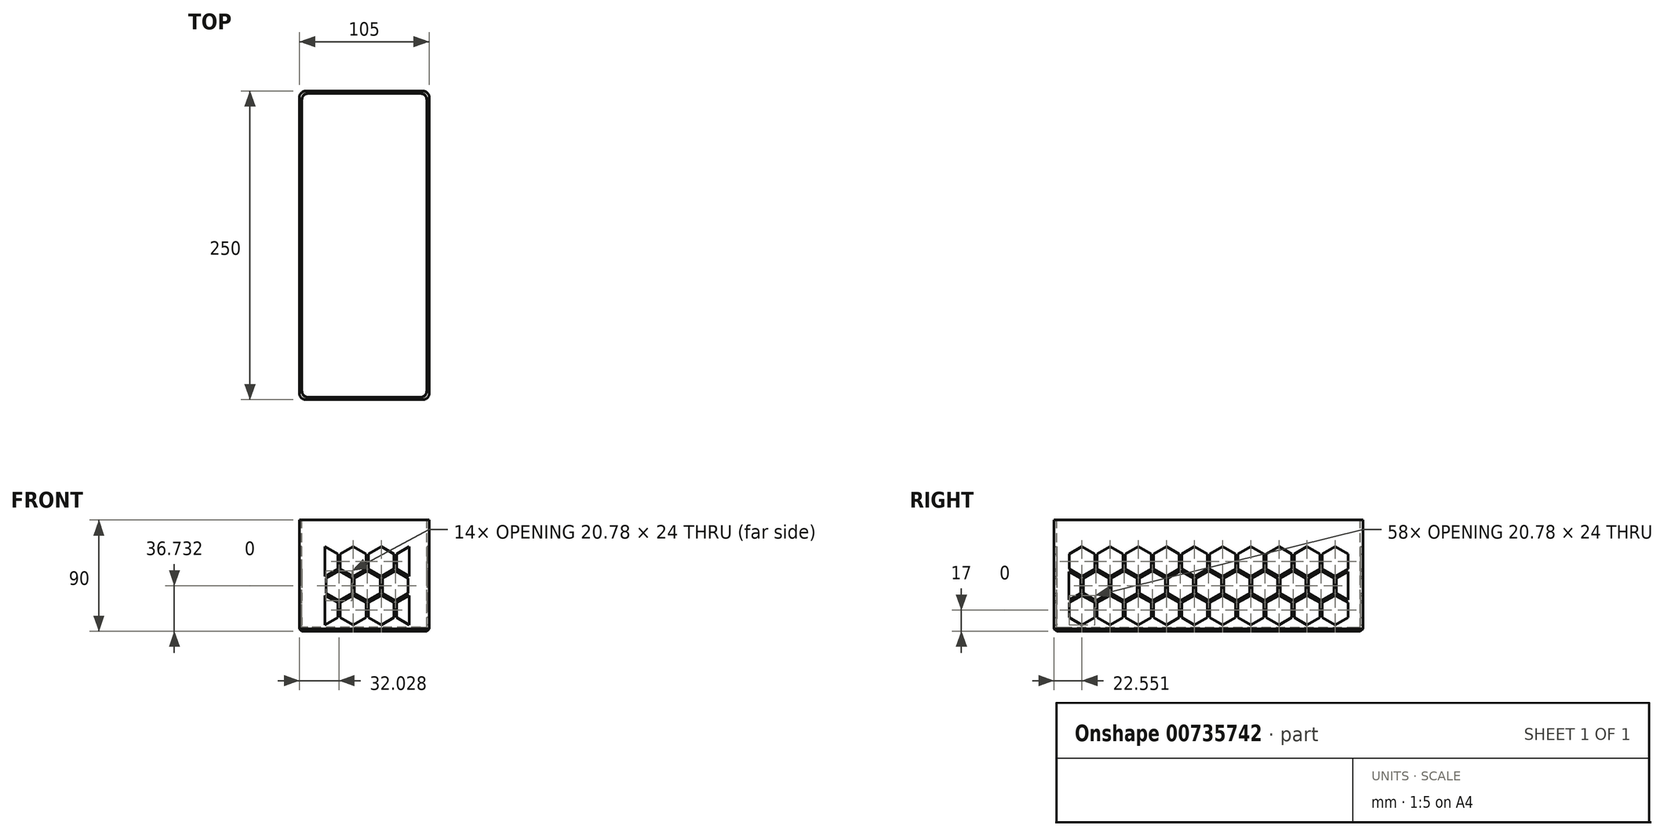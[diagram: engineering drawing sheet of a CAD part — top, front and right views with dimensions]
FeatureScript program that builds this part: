
annotation { "Feature Type Name" : "Feature", "Feature Type Description" : "" }
export const myFeature = defineFeature(function(context is Context, id is Id, definition is map)
    precondition{}
    {
        {
            var Q0;
            Q0=qCreatedBy(makeId("Top.planeOp"),FACE);
            var sketch = newSketch(context, id + "F0", { "sketchPlane" : qUnion([Q0])});
            skLineSegment(sketch, "E0.bottom", {"start": v(-56.87, 197.97) * mm, "end": v(48.13, 197.97) * mm});
            skLineSegment(sketch, "E0.top", {"start": v(-56.87, -52.03) * mm, "end": v(48.13, -52.03) * mm});
            skLineSegment(sketch, "E0.left", {"start": v(-56.87, 197.97) * mm, "end": v(-56.87, -52.03) * mm});
            skLineSegment(sketch, "E0.right", {"start": v(48.13, 197.97) * mm, "end": v(48.13, -52.03) * mm});
            skSolve(sketch);
        }
        {
            var Q0;
            Q0 = qSketchRegion(id + "F0", true);
            extrude(context, id + "F1", {"entities" : qUnion([Q0]), "depth" : 90 * mm, "offsetDistance" : 25 * mm});
        }
        {
            var Q0;
            Q0=makeQuery(id+"F1.opExtrude","CAP_FACE",FACE,{"disambiguationData":[OSD([sQuery(id+"F0.wireOp",EDGE,"E0.bottom"),sQuery(id+"F0.wireOp",EDGE,"E0.top"),sQuery(id+"F0.wireOp",EDGE,"E0.left"),sQuery(id+"F0.wireOp",EDGE,"E0.right")])],"isStart":false});
            var sketch = newSketch(context, id + "F2", { "sketchPlane" : qUnion([Q0])});
            skLineSegment(sketch, "E1.bottom", {"start": v(46.13, -50.03) * mm, "end": v(-54.87, -50.03) * mm});
            skLineSegment(sketch, "E1.top", {"start": v(46.13, 195.97) * mm, "end": v(-54.87, 195.97) * mm});
            skLineSegment(sketch, "E1.left", {"start": v(46.13, -50.03) * mm, "end": v(46.13, 195.97) * mm});
            skLineSegment(sketch, "E1.right", {"start": v(-54.87, -50.03) * mm, "end": v(-54.87, 195.97) * mm});
            skSolve(sketch);
        }
        {
            var Q0;
            Q0 = qSketchRegion(id + "F2", true);
            extrude(context, id + "F3", {"entities" : qUnion([Q0]), "operationType" : NewBodyOperationType.REMOVE, "oppositeDirection" : true, "depth" : 87 * mm, "offsetDistance" : 25 * mm});
        }
        {
            var Q0;
            Q0=makeQuery(id+"F1.opExtrude","SWEPT_EDGE",EDGE,{"disambiguationData":[OSD([sQuery(id+"F0.wireOp",EDGE,"E0.top"),sQuery(id+"F0.wireOp",EDGE,"E0.right")])]});
            var Q1;
            Q1=makeQuery(id+"F1.opExtrude","SWEPT_EDGE",EDGE,{"disambiguationData":[OSD([sQuery(id+"F0.wireOp",EDGE,"E0.top"),sQuery(id+"F0.wireOp",EDGE,"E0.left")])]});
            var Q2;
            Q2=makeQuery(id+"F1.opExtrude","SWEPT_EDGE",EDGE,{"disambiguationData":[OSD([sQuery(id+"F0.wireOp",EDGE,"E0.bottom"),sQuery(id+"F0.wireOp",EDGE,"E0.right")])]});
            var Q3;
            Q3=makeQuery(id+"F1.opExtrude","SWEPT_EDGE",EDGE,{"disambiguationData":[OSD([sQuery(id+"F0.wireOp",EDGE,"E0.bottom"),sQuery(id+"F0.wireOp",EDGE,"E0.left")])]});
            fillet(context, id + "F4", {"entities" : qUnion([Q0, Q1, Q2, Q3]), "radius" : 5 * mm, "tangentPropagation" : true, "allowEdgeOverflow" : false});
        }
        {
            var Q0;
            Q0=makeQuery(id+"F3.boolean.opBoolean","COPY",EDGE,{"derivedFrom":makeQuery(id+"F3.opExtrude","SWEPT_EDGE",EDGE,{"disambiguationData":[OSD([sQuery(id+"F2.wireOp",EDGE,"E1.top"),sQuery(id+"F2.wireOp",EDGE,"E1.right")])]})});
            var Q1;
            Q1=makeQuery(id+"F3.boolean.opBoolean","COPY",EDGE,{"derivedFrom":makeQuery(id+"F3.opExtrude","SWEPT_EDGE",EDGE,{"disambiguationData":[OSD([sQuery(id+"F2.wireOp",EDGE,"E1.top"),sQuery(id+"F2.wireOp",EDGE,"E1.left")])]})});
            var Q2;
            Q2=makeQuery(id+"F3.boolean.opBoolean","COPY",EDGE,{"derivedFrom":makeQuery(id+"F3.opExtrude","SWEPT_EDGE",EDGE,{"disambiguationData":[OSD([sQuery(id+"F2.wireOp",EDGE,"E1.bottom"),sQuery(id+"F2.wireOp",EDGE,"E1.right")])]})});
            var Q3;
            Q3=makeQuery(id+"F3.boolean.opBoolean","COPY",EDGE,{"derivedFrom":makeQuery(id+"F3.opExtrude","SWEPT_EDGE",EDGE,{"disambiguationData":[OSD([sQuery(id+"F2.wireOp",EDGE,"E1.bottom"),sQuery(id+"F2.wireOp",EDGE,"E1.left")])]})});
            fillet(context, id + "F5", {"entities" : qUnion([Q0, Q1, Q2, Q3]), "radius" : 5 * mm, "tangentPropagation" : true, "allowEdgeOverflow" : false});
        }
        {
            var Q0;
            Q0=makeQuery(id+"F1.opExtrude","CAP_FACE",FACE,{"disambiguationData":[OSD([sQuery(id+"F0.wireOp",EDGE,"E0.bottom"),sQuery(id+"F0.wireOp",EDGE,"E0.top"),sQuery(id+"F0.wireOp",EDGE,"E0.left"),sQuery(id+"F0.wireOp",EDGE,"E0.right")])],"isStart":true});
            chamfer(context, id + "F6", {"entities" : qUnion([Q0]), "width" : 2 * mm, "tangentPropagation" : true});
        }
        {
            var Q0;
            Q0=makeQuery(id+"F1.opExtrude","SWEPT_FACE",FACE,{"disambiguationData":[OSD([sQuery(id+"F0.wireOp",EDGE,"E0.left")])]});
            var sketch = newSketch(context, id + "F7", { "sketchPlane" : qUnion([Q0])});
            skLineSegment(sketch, "E2", {"start": v(-185.97, 68.46) * mm, "end": v(-185.97, -21.54) * mm, "construction": true});
            skLineSegment(sketch, "E3", {"start": v(-185.97, 68.46) * mm, "end": v(74.03, 68.46) * mm, "construction": true});
            skLineSegment(sketch, "E4", {"start": v(40.03, 68.46) * mm, "end": v(40.03, -21.54) * mm});
            skCircle(sketch, "E5.cCircle", {"center": v(-175.58, 56.46) * mm, "radius": 10.4 * mm, "construction": true});
            skLineSegment(sketch, "E5.0", {"start": v(-165.2, 50.46) * mm, "end": v(-175.58, 44.46) * mm});
            skLineSegment(sketch, "E5.1", {"start": v(-175.58, 44.46) * mm, "end": v(-185.97, 50.46) * mm});
            skLineSegment(sketch, "E5.2", {"start": v(-185.97, 50.46) * mm, "end": v(-185.97, 62.46) * mm});
            skLineSegment(sketch, "E5.3", {"start": v(-185.97, 62.46) * mm, "end": v(-175.58, 68.46) * mm});
            skLineSegment(sketch, "E5.4", {"start": v(-175.58, 68.46) * mm, "end": v(-165.2, 62.46) * mm});
            skLineSegment(sketch, "E5.5", {"start": v(-165.2, 62.46) * mm, "end": v(-165.2, 50.46) * mm});
            skPoint(sketch, "E5.0.midPoint", {"position": v(-170.39, 47.46) * mm});
            skCircle(sketch, "E6.cCircle", {"center": v(-152.8, 56.46) * mm, "radius": 10.4 * mm, "construction": true});
            skLineSegment(sketch, "E6.0", {"start": v(-142.4, 50.46) * mm, "end": v(-152.8, 44.46) * mm});
            skLineSegment(sketch, "E6.1", {"start": v(-152.8, 44.46) * mm, "end": v(-163.2, 50.46) * mm});
            skLineSegment(sketch, "E6.2", {"start": v(-163.2, 50.46) * mm, "end": v(-163.2, 62.46) * mm});
            skLineSegment(sketch, "E6.3", {"start": v(-163.2, 62.46) * mm, "end": v(-152.8, 68.46) * mm});
            skLineSegment(sketch, "E6.4", {"start": v(-152.8, 68.46) * mm, "end": v(-142.4, 62.46) * mm});
            skLineSegment(sketch, "E6.5", {"start": v(-142.4, 62.46) * mm, "end": v(-142.4, 50.46) * mm});
            skPoint(sketch, "E6.0.midPoint", {"position": v(-147.6, 47.46) * mm});
            skLineSegment(sketch, "E7", {"start": v(68.97, 44.46) * mm, "end": v(-241.4, 44.46) * mm, "construction": true});
            skCircle(sketch, "E8.cCircle", {"center": v(-130.01, 56.46) * mm, "radius": 10.4 * mm, "construction": true});
            skLineSegment(sketch, "E8.0", {"start": v(-119.62, 50.46) * mm, "end": v(-130.01, 44.46) * mm});
            skLineSegment(sketch, "E8.1", {"start": v(-130.01, 44.46) * mm, "end": v(-140.4, 50.46) * mm});
            skLineSegment(sketch, "E8.2", {"start": v(-140.4, 50.46) * mm, "end": v(-140.4, 62.46) * mm});
            skLineSegment(sketch, "E8.3", {"start": v(-140.4, 62.46) * mm, "end": v(-130.01, 68.46) * mm});
            skLineSegment(sketch, "E8.4", {"start": v(-130.01, 68.46) * mm, "end": v(-119.62, 62.46) * mm});
            skLineSegment(sketch, "E8.5", {"start": v(-119.62, 62.46) * mm, "end": v(-119.62, 50.46) * mm});
            skPoint(sketch, "E8.0.midPoint", {"position": v(-124.82, 47.46) * mm});
            skCircle(sketch, "E9.cCircle", {"center": v(-107.23, 56.46) * mm, "radius": 10.4 * mm, "construction": true});
            skLineSegment(sketch, "E9.0", {"start": v(-96.84, 50.46) * mm, "end": v(-107.23, 44.46) * mm});
            skLineSegment(sketch, "E9.1", {"start": v(-107.23, 44.46) * mm, "end": v(-117.62, 50.46) * mm});
            skLineSegment(sketch, "E9.2", {"start": v(-117.62, 50.46) * mm, "end": v(-117.62, 62.46) * mm});
            skLineSegment(sketch, "E9.3", {"start": v(-117.62, 62.46) * mm, "end": v(-107.23, 68.46) * mm});
            skLineSegment(sketch, "E9.4", {"start": v(-107.23, 68.46) * mm, "end": v(-96.84, 62.46) * mm});
            skLineSegment(sketch, "E9.5", {"start": v(-96.84, 62.46) * mm, "end": v(-96.84, 50.46) * mm});
            skPoint(sketch, "E9.0.midPoint", {"position": v(-102.03, 47.46) * mm});
            skCircle(sketch, "E10.cCircle", {"center": v(-84.44, 56.46) * mm, "radius": 10.4 * mm, "construction": true});
            skLineSegment(sketch, "E10.0", {"start": v(-74.05, 50.46) * mm, "end": v(-84.44, 44.46) * mm});
            skLineSegment(sketch, "E10.1", {"start": v(-84.44, 44.46) * mm, "end": v(-94.84, 50.46) * mm});
            skLineSegment(sketch, "E10.2", {"start": v(-94.84, 50.46) * mm, "end": v(-94.84, 62.46) * mm});
            skLineSegment(sketch, "E10.3", {"start": v(-94.84, 62.46) * mm, "end": v(-84.44, 68.46) * mm});
            skLineSegment(sketch, "E10.4", {"start": v(-84.44, 68.46) * mm, "end": v(-74.05, 62.46) * mm});
            skLineSegment(sketch, "E10.5", {"start": v(-74.05, 62.46) * mm, "end": v(-74.05, 50.46) * mm});
            skPoint(sketch, "E10.0.midPoint", {"position": v(-79.25, 47.46) * mm});
            skCircle(sketch, "E11.cCircle", {"center": v(-61.66, 56.46) * mm, "radius": 10.4 * mm, "construction": true});
            skLineSegment(sketch, "E11.0", {"start": v(-51.27, 50.46) * mm, "end": v(-61.66, 44.46) * mm});
            skLineSegment(sketch, "E11.1", {"start": v(-61.66, 44.46) * mm, "end": v(-72.05, 50.46) * mm});
            skLineSegment(sketch, "E11.2", {"start": v(-72.05, 50.46) * mm, "end": v(-72.05, 62.46) * mm});
            skLineSegment(sketch, "E11.3", {"start": v(-72.05, 62.46) * mm, "end": v(-61.66, 68.46) * mm});
            skLineSegment(sketch, "E11.4", {"start": v(-61.66, 68.46) * mm, "end": v(-51.27, 62.46) * mm});
            skLineSegment(sketch, "E11.5", {"start": v(-51.27, 62.46) * mm, "end": v(-51.27, 50.46) * mm});
            skPoint(sketch, "E11.0.midPoint", {"position": v(-56.46, 47.46) * mm});
            skCircle(sketch, "E12.cCircle", {"center": v(-38.87, 56.46) * mm, "radius": 10.4 * mm, "construction": true});
            skLineSegment(sketch, "E12.0", {"start": v(-28.48, 50.46) * mm, "end": v(-38.87, 44.46) * mm});
            skLineSegment(sketch, "E12.1", {"start": v(-38.87, 44.46) * mm, "end": v(-49.27, 50.46) * mm});
            skLineSegment(sketch, "E12.2", {"start": v(-49.27, 50.46) * mm, "end": v(-49.27, 62.46) * mm});
            skLineSegment(sketch, "E12.3", {"start": v(-49.27, 62.46) * mm, "end": v(-38.87, 68.46) * mm});
            skLineSegment(sketch, "E12.4", {"start": v(-38.87, 68.46) * mm, "end": v(-28.48, 62.46) * mm});
            skLineSegment(sketch, "E12.5", {"start": v(-28.48, 62.46) * mm, "end": v(-28.48, 50.46) * mm});
            skPoint(sketch, "E12.0.midPoint", {"position": v(-33.68, 47.46) * mm});
            skCircle(sketch, "E13.cCircle", {"center": v(-16.1, 56.46) * mm, "radius": 10.4 * mm, "construction": true});
            skLineSegment(sketch, "E13.0", {"start": v(-5.7, 50.46) * mm, "end": v(-16.1, 44.46) * mm});
            skLineSegment(sketch, "E13.1", {"start": v(-16.1, 44.46) * mm, "end": v(-26.48, 50.46) * mm});
            skLineSegment(sketch, "E13.2", {"start": v(-26.48, 50.46) * mm, "end": v(-26.48, 62.46) * mm});
            skLineSegment(sketch, "E13.3", {"start": v(-26.48, 62.46) * mm, "end": v(-16.1, 68.46) * mm});
            skLineSegment(sketch, "E13.4", {"start": v(-16.1, 68.46) * mm, "end": v(-5.7, 62.46) * mm});
            skLineSegment(sketch, "E13.5", {"start": v(-5.7, 62.46) * mm, "end": v(-5.7, 50.46) * mm});
            skPoint(sketch, "E13.0.midPoint", {"position": v(-10.9, 47.46) * mm});
            skCircle(sketch, "E14.cCircle", {"center": v(6.7, 56.46) * mm, "radius": 10.4 * mm, "construction": true});
            skLineSegment(sketch, "E14.0", {"start": v(17.09, 50.46) * mm, "end": v(6.7, 44.46) * mm});
            skLineSegment(sketch, "E14.1", {"start": v(6.7, 44.46) * mm, "end": v(-3.7, 50.46) * mm});
            skLineSegment(sketch, "E14.2", {"start": v(-3.7, 50.46) * mm, "end": v(-3.7, 62.46) * mm});
            skLineSegment(sketch, "E14.3", {"start": v(-3.7, 62.46) * mm, "end": v(6.7, 68.46) * mm});
            skLineSegment(sketch, "E14.4", {"start": v(6.7, 68.46) * mm, "end": v(17.09, 62.46) * mm});
            skLineSegment(sketch, "E14.5", {"start": v(17.09, 62.46) * mm, "end": v(17.09, 50.46) * mm});
            skPoint(sketch, "E14.0.midPoint", {"position": v(11.9, 47.46) * mm});
            skCircle(sketch, "E15.cCircle", {"center": v(29.48, 56.46) * mm, "radius": 10.4 * mm, "construction": true});
            skLineSegment(sketch, "E15.0", {"start": v(39.87, 50.46) * mm, "end": v(29.48, 44.46) * mm});
            skLineSegment(sketch, "E15.1", {"start": v(29.48, 44.46) * mm, "end": v(19.09, 50.46) * mm});
            skLineSegment(sketch, "E15.2", {"start": v(19.09, 50.46) * mm, "end": v(19.09, 62.46) * mm});
            skLineSegment(sketch, "E15.3", {"start": v(19.09, 62.46) * mm, "end": v(29.48, 68.46) * mm});
            skLineSegment(sketch, "E15.4", {"start": v(29.48, 68.46) * mm, "end": v(39.87, 62.46) * mm});
            skLineSegment(sketch, "E15.5", {"start": v(39.87, 62.46) * mm, "end": v(39.87, 50.46) * mm});
            skPoint(sketch, "E15.0.midPoint", {"position": v(34.68, 47.46) * mm});
            skArc(sketch, "E16.cCircle", {"start": v(-185.97, 26.39) * mm, "mid": v(-176.58, 36.73) * mm, "end": v(-185.97, 47.08) * mm, "construction": true});
            skLineSegment(sketch, "E16.0", {"start": v(-176.58, 30.73) * mm, "end": v(-185.97, 25.3) * mm});
            skLineSegment(sketch, "E16.4", {"start": v(-185.97, 48.15) * mm, "end": v(-176.58, 42.73) * mm});
            skLineSegment(sketch, "E16.5", {"start": v(-176.58, 42.73) * mm, "end": v(-176.58, 30.73) * mm});
            skPoint(sketch, "E16.0.midPoint", {"position": v(-181.78, 27.73) * mm});
            skCircle(sketch, "E17.cCircle", {"center": v(-141.4, 36.73) * mm, "radius": 10.4 * mm, "construction": true});
            skLineSegment(sketch, "E17.0", {"start": v(-131.01, 30.73) * mm, "end": v(-141.4, 24.73) * mm});
            skLineSegment(sketch, "E17.1", {"start": v(-141.4, 24.73) * mm, "end": v(-151.8, 30.73) * mm});
            skLineSegment(sketch, "E17.2", {"start": v(-151.8, 30.73) * mm, "end": v(-151.8, 42.73) * mm});
            skLineSegment(sketch, "E17.3", {"start": v(-151.8, 42.73) * mm, "end": v(-141.4, 48.73) * mm});
            skLineSegment(sketch, "E17.4", {"start": v(-141.4, 48.73) * mm, "end": v(-131.01, 42.73) * mm});
            skLineSegment(sketch, "E17.5", {"start": v(-131.01, 42.73) * mm, "end": v(-131.01, 30.73) * mm});
            skPoint(sketch, "E17.0.midPoint", {"position": v(-136.2, 27.73) * mm});
            skCircle(sketch, "E18.cCircle", {"center": v(-118.62, 36.73) * mm, "radius": 10.4 * mm, "construction": true});
            skLineSegment(sketch, "E18.0", {"start": v(-108.23, 30.73) * mm, "end": v(-118.62, 24.73) * mm});
            skLineSegment(sketch, "E18.1", {"start": v(-118.62, 24.73) * mm, "end": v(-129.01, 30.73) * mm});
            skLineSegment(sketch, "E18.2", {"start": v(-129.01, 30.73) * mm, "end": v(-129.01, 42.73) * mm});
            skLineSegment(sketch, "E18.3", {"start": v(-129.01, 42.73) * mm, "end": v(-118.62, 48.73) * mm});
            skLineSegment(sketch, "E18.4", {"start": v(-118.62, 48.73) * mm, "end": v(-108.23, 42.73) * mm});
            skLineSegment(sketch, "E18.5", {"start": v(-108.23, 42.73) * mm, "end": v(-108.23, 30.73) * mm});
            skPoint(sketch, "E18.0.midPoint", {"position": v(-113.42, 27.73) * mm});
            skCircle(sketch, "E19.cCircle", {"center": v(-95.84, 36.73) * mm, "radius": 10.4 * mm, "construction": true});
            skLineSegment(sketch, "E19.0", {"start": v(-85.44, 30.73) * mm, "end": v(-95.84, 24.73) * mm});
            skLineSegment(sketch, "E19.1", {"start": v(-95.84, 24.73) * mm, "end": v(-106.23, 30.73) * mm});
            skLineSegment(sketch, "E19.2", {"start": v(-106.23, 30.73) * mm, "end": v(-106.23, 42.73) * mm});
            skLineSegment(sketch, "E19.3", {"start": v(-106.23, 42.73) * mm, "end": v(-95.84, 48.73) * mm});
            skLineSegment(sketch, "E19.4", {"start": v(-95.84, 48.73) * mm, "end": v(-85.44, 42.73) * mm});
            skLineSegment(sketch, "E19.5", {"start": v(-85.44, 42.73) * mm, "end": v(-85.44, 30.73) * mm});
            skPoint(sketch, "E19.0.midPoint", {"position": v(-90.64, 27.73) * mm});
            skCircle(sketch, "E20.cCircle", {"center": v(-73.05, 36.73) * mm, "radius": 10.4 * mm, "construction": true});
            skLineSegment(sketch, "E20.0", {"start": v(-62.66, 30.73) * mm, "end": v(-73.05, 24.73) * mm});
            skLineSegment(sketch, "E20.1", {"start": v(-73.05, 24.73) * mm, "end": v(-83.44, 30.73) * mm});
            skLineSegment(sketch, "E20.2", {"start": v(-83.44, 30.73) * mm, "end": v(-83.44, 42.73) * mm});
            skLineSegment(sketch, "E20.3", {"start": v(-83.44, 42.73) * mm, "end": v(-73.05, 48.73) * mm});
            skLineSegment(sketch, "E20.4", {"start": v(-73.05, 48.73) * mm, "end": v(-62.66, 42.73) * mm});
            skLineSegment(sketch, "E20.5", {"start": v(-62.66, 42.73) * mm, "end": v(-62.66, 30.73) * mm});
            skPoint(sketch, "E20.0.midPoint", {"position": v(-67.86, 27.73) * mm});
            skCircle(sketch, "E21.cCircle", {"center": v(-50.27, 36.73) * mm, "radius": 10.4 * mm, "construction": true});
            skLineSegment(sketch, "E21.0", {"start": v(-39.87, 30.73) * mm, "end": v(-50.27, 24.73) * mm});
            skLineSegment(sketch, "E21.1", {"start": v(-50.27, 24.73) * mm, "end": v(-60.66, 30.73) * mm});
            skLineSegment(sketch, "E21.2", {"start": v(-60.66, 30.73) * mm, "end": v(-60.66, 42.73) * mm});
            skLineSegment(sketch, "E21.3", {"start": v(-60.66, 42.73) * mm, "end": v(-50.27, 48.73) * mm});
            skLineSegment(sketch, "E21.4", {"start": v(-50.27, 48.73) * mm, "end": v(-39.87, 42.73) * mm});
            skLineSegment(sketch, "E21.5", {"start": v(-39.87, 42.73) * mm, "end": v(-39.87, 30.73) * mm});
            skPoint(sketch, "E21.0.midPoint", {"position": v(-45.07, 27.73) * mm});
            skCircle(sketch, "E22.cCircle", {"center": v(-27.48, 36.73) * mm, "radius": 10.4 * mm, "construction": true});
            skLineSegment(sketch, "E22.0", {"start": v(-17.1, 30.73) * mm, "end": v(-27.48, 24.73) * mm});
            skLineSegment(sketch, "E22.1", {"start": v(-27.48, 24.73) * mm, "end": v(-37.87, 30.73) * mm});
            skLineSegment(sketch, "E22.2", {"start": v(-37.87, 30.73) * mm, "end": v(-37.87, 42.73) * mm});
            skLineSegment(sketch, "E22.3", {"start": v(-37.87, 42.73) * mm, "end": v(-27.48, 48.73) * mm});
            skLineSegment(sketch, "E22.4", {"start": v(-27.48, 48.73) * mm, "end": v(-17.1, 42.73) * mm});
            skLineSegment(sketch, "E22.5", {"start": v(-17.1, 42.73) * mm, "end": v(-17.1, 30.73) * mm});
            skPoint(sketch, "E22.0.midPoint", {"position": v(-22.29, 27.73) * mm});
            skCircle(sketch, "E23.cCircle", {"center": v(-4.7, 36.73) * mm, "radius": 10.4 * mm, "construction": true});
            skLineSegment(sketch, "E23.0", {"start": v(5.7, 30.73) * mm, "end": v(-4.7, 24.73) * mm});
            skLineSegment(sketch, "E23.1", {"start": v(-4.7, 24.73) * mm, "end": v(-15.1, 30.73) * mm});
            skLineSegment(sketch, "E23.2", {"start": v(-15.1, 30.73) * mm, "end": v(-15.1, 42.73) * mm});
            skLineSegment(sketch, "E23.3", {"start": v(-15.1, 42.73) * mm, "end": v(-4.7, 48.73) * mm});
            skLineSegment(sketch, "E23.4", {"start": v(-4.7, 48.73) * mm, "end": v(5.7, 42.73) * mm});
            skLineSegment(sketch, "E23.5", {"start": v(5.7, 42.73) * mm, "end": v(5.7, 30.73) * mm});
            skPoint(sketch, "E23.0.midPoint", {"position": v(0.5, 27.73) * mm});
            skCircle(sketch, "E24.cCircle", {"center": v(18.09, 36.73) * mm, "radius": 10.4 * mm, "construction": true});
            skLineSegment(sketch, "E24.0", {"start": v(28.48, 30.73) * mm, "end": v(18.09, 24.73) * mm});
            skLineSegment(sketch, "E24.1", {"start": v(18.09, 24.73) * mm, "end": v(7.7, 30.73) * mm});
            skLineSegment(sketch, "E24.2", {"start": v(7.7, 30.73) * mm, "end": v(7.7, 42.73) * mm});
            skLineSegment(sketch, "E24.3", {"start": v(7.7, 42.73) * mm, "end": v(18.09, 48.73) * mm});
            skLineSegment(sketch, "E24.4", {"start": v(18.09, 48.73) * mm, "end": v(28.48, 42.73) * mm});
            skLineSegment(sketch, "E24.5", {"start": v(28.48, 42.73) * mm, "end": v(28.48, 30.73) * mm});
            skPoint(sketch, "E24.0.midPoint", {"position": v(23.28, 27.73) * mm});
            skLineSegment(sketch, "E25", {"start": v(74.03, 48.73) * mm, "end": v(-185.97, 48.73) * mm, "construction": true});
            skCircle(sketch, "E26.cCircle", {"center": v(-164.2, 36.73) * mm, "radius": 10.4 * mm, "construction": true});
            skLineSegment(sketch, "E26.0", {"start": v(-153.8, 30.73) * mm, "end": v(-164.2, 24.73) * mm});
            skLineSegment(sketch, "E26.1", {"start": v(-164.2, 24.73) * mm, "end": v(-174.58, 30.73) * mm});
            skLineSegment(sketch, "E26.2", {"start": v(-174.58, 30.73) * mm, "end": v(-174.58, 42.73) * mm});
            skLineSegment(sketch, "E26.3", {"start": v(-174.58, 42.73) * mm, "end": v(-164.2, 48.73) * mm});
            skLineSegment(sketch, "E26.4", {"start": v(-164.2, 48.73) * mm, "end": v(-153.8, 42.73) * mm});
            skLineSegment(sketch, "E26.5", {"start": v(-153.8, 42.73) * mm, "end": v(-153.8, 30.73) * mm});
            skPoint(sketch, "E26.0.midPoint", {"position": v(-159, 27.73) * mm});
            skLineSegment(sketch, "E27", {"start": v(-189.97, 24.73) * mm, "end": v(75.25, 24.73) * mm, "construction": true});
            skArc(sketch, "E28.cCircle", {"start": v(40.03, 47.09) * mm, "mid": v(30.48, 36.73) * mm, "end": v(40.03, 26.37) * mm, "construction": true});
            skLineSegment(sketch, "E28.1", {"start": v(40.87, 24.73) * mm, "end": v(30.48, 30.73) * mm});
            skLineSegment(sketch, "E28.2", {"start": v(30.48, 30.73) * mm, "end": v(30.48, 42.73) * mm});
            skLineSegment(sketch, "E28.3", {"start": v(30.48, 42.73) * mm, "end": v(40.03, 48.24) * mm});
            skPoint(sketch, "E28.0.midPoint", {"position": v(46.07, 27.73) * mm});
            skCircle(sketch, "E29.cCircle", {"center": v(-175.58, 17) * mm, "radius": 10.4 * mm, "construction": true});
            skLineSegment(sketch, "E29.0", {"start": v(-165.2, 11) * mm, "end": v(-175.58, 5) * mm});
            skLineSegment(sketch, "E29.1", {"start": v(-175.58, 5) * mm, "end": v(-185.97, 11) * mm});
            skLineSegment(sketch, "E29.2", {"start": v(-185.97, 11) * mm, "end": v(-185.97, 23) * mm});
            skLineSegment(sketch, "E29.3", {"start": v(-185.97, 23) * mm, "end": v(-175.58, 29) * mm});
            skLineSegment(sketch, "E29.4", {"start": v(-175.58, 29) * mm, "end": v(-165.2, 23) * mm});
            skLineSegment(sketch, "E29.5", {"start": v(-165.2, 23) * mm, "end": v(-165.2, 11) * mm});
            skPoint(sketch, "E29.0.midPoint", {"position": v(-170.39, 8) * mm});
            skLineSegment(sketch, "E30", {"start": v(-185.97, 29) * mm, "end": v(74.03, 29) * mm, "construction": true});
            skLineSegment(sketch, "E31", {"start": v(-185.97, 5) * mm, "end": v(74.03, 5) * mm, "construction": true});
            skCircle(sketch, "E32.cCircle", {"center": v(-152.8, 17) * mm, "radius": 10.4 * mm, "construction": true});
            skLineSegment(sketch, "E32.0", {"start": v(-142.4, 11) * mm, "end": v(-152.8, 5) * mm});
            skLineSegment(sketch, "E32.1", {"start": v(-152.8, 5) * mm, "end": v(-163.2, 11) * mm});
            skLineSegment(sketch, "E32.2", {"start": v(-163.2, 11) * mm, "end": v(-163.2, 23) * mm});
            skLineSegment(sketch, "E32.3", {"start": v(-163.2, 23) * mm, "end": v(-152.8, 29) * mm});
            skLineSegment(sketch, "E32.4", {"start": v(-152.8, 29) * mm, "end": v(-142.4, 23) * mm});
            skLineSegment(sketch, "E32.5", {"start": v(-142.4, 23) * mm, "end": v(-142.4, 11) * mm});
            skPoint(sketch, "E32.0.midPoint", {"position": v(-147.6, 8) * mm});
            skCircle(sketch, "E33.cCircle", {"center": v(-130.01, 17) * mm, "radius": 10.4 * mm, "construction": true});
            skLineSegment(sketch, "E33.0", {"start": v(-119.62, 11) * mm, "end": v(-130.01, 5) * mm});
            skLineSegment(sketch, "E33.1", {"start": v(-130.01, 5) * mm, "end": v(-140.4, 11) * mm});
            skLineSegment(sketch, "E33.2", {"start": v(-140.4, 11) * mm, "end": v(-140.4, 23) * mm});
            skLineSegment(sketch, "E33.3", {"start": v(-140.4, 23) * mm, "end": v(-130.01, 29) * mm});
            skLineSegment(sketch, "E33.4", {"start": v(-130.01, 29) * mm, "end": v(-119.62, 23) * mm});
            skLineSegment(sketch, "E33.5", {"start": v(-119.62, 23) * mm, "end": v(-119.62, 11) * mm});
            skPoint(sketch, "E33.0.midPoint", {"position": v(-124.82, 8) * mm});
            skCircle(sketch, "E34.cCircle", {"center": v(-107.23, 17) * mm, "radius": 10.4 * mm, "construction": true});
            skLineSegment(sketch, "E34.0", {"start": v(-96.84, 11) * mm, "end": v(-107.23, 5) * mm});
            skLineSegment(sketch, "E34.1", {"start": v(-107.23, 5) * mm, "end": v(-117.62, 11) * mm});
            skLineSegment(sketch, "E34.2", {"start": v(-117.62, 11) * mm, "end": v(-117.62, 23) * mm});
            skLineSegment(sketch, "E34.3", {"start": v(-117.62, 23) * mm, "end": v(-107.23, 29) * mm});
            skLineSegment(sketch, "E34.4", {"start": v(-107.23, 29) * mm, "end": v(-96.84, 23) * mm});
            skLineSegment(sketch, "E34.5", {"start": v(-96.84, 23) * mm, "end": v(-96.84, 11) * mm});
            skPoint(sketch, "E34.0.midPoint", {"position": v(-102.03, 8) * mm});
            skCircle(sketch, "E35.cCircle", {"center": v(-84.44, 17) * mm, "radius": 10.4 * mm, "construction": true});
            skLineSegment(sketch, "E35.0", {"start": v(-74.05, 11) * mm, "end": v(-84.44, 5) * mm});
            skLineSegment(sketch, "E35.1", {"start": v(-84.44, 5) * mm, "end": v(-94.84, 11) * mm});
            skLineSegment(sketch, "E35.2", {"start": v(-94.84, 11) * mm, "end": v(-94.84, 23) * mm});
            skLineSegment(sketch, "E35.3", {"start": v(-94.84, 23) * mm, "end": v(-84.44, 29) * mm});
            skLineSegment(sketch, "E35.4", {"start": v(-84.44, 29) * mm, "end": v(-74.05, 23) * mm});
            skLineSegment(sketch, "E35.5", {"start": v(-74.05, 23) * mm, "end": v(-74.05, 11) * mm});
            skPoint(sketch, "E35.0.midPoint", {"position": v(-79.25, 8) * mm});
            skCircle(sketch, "E36.cCircle", {"center": v(-61.66, 17) * mm, "radius": 10.4 * mm, "construction": true});
            skLineSegment(sketch, "E36.0", {"start": v(-51.27, 11) * mm, "end": v(-61.66, 5) * mm});
            skLineSegment(sketch, "E36.1", {"start": v(-61.66, 5) * mm, "end": v(-72.05, 11) * mm});
            skLineSegment(sketch, "E36.2", {"start": v(-72.05, 11) * mm, "end": v(-72.05, 23) * mm});
            skLineSegment(sketch, "E36.3", {"start": v(-72.05, 23) * mm, "end": v(-61.66, 29) * mm});
            skLineSegment(sketch, "E36.4", {"start": v(-61.66, 29) * mm, "end": v(-51.27, 23) * mm});
            skLineSegment(sketch, "E36.5", {"start": v(-51.27, 23) * mm, "end": v(-51.27, 11) * mm});
            skPoint(sketch, "E36.0.midPoint", {"position": v(-56.46, 8) * mm});
            skCircle(sketch, "E37.cCircle", {"center": v(-38.87, 17) * mm, "radius": 10.4 * mm, "construction": true});
            skLineSegment(sketch, "E37.0", {"start": v(-28.48, 11) * mm, "end": v(-38.87, 5) * mm});
            skLineSegment(sketch, "E37.1", {"start": v(-38.87, 5) * mm, "end": v(-49.27, 11) * mm});
            skLineSegment(sketch, "E37.2", {"start": v(-49.27, 11) * mm, "end": v(-49.27, 23) * mm});
            skLineSegment(sketch, "E37.3", {"start": v(-49.27, 23) * mm, "end": v(-38.87, 29) * mm});
            skLineSegment(sketch, "E37.4", {"start": v(-38.87, 29) * mm, "end": v(-28.48, 23) * mm});
            skLineSegment(sketch, "E37.5", {"start": v(-28.48, 23) * mm, "end": v(-28.48, 11) * mm});
            skPoint(sketch, "E37.0.midPoint", {"position": v(-33.68, 8) * mm});
            skCircle(sketch, "E38.cCircle", {"center": v(-16.1, 17) * mm, "radius": 10.4 * mm, "construction": true});
            skLineSegment(sketch, "E38.0", {"start": v(-5.7, 11) * mm, "end": v(-16.1, 5) * mm});
            skLineSegment(sketch, "E38.1", {"start": v(-16.1, 5) * mm, "end": v(-26.48, 11) * mm});
            skLineSegment(sketch, "E38.2", {"start": v(-26.48, 11) * mm, "end": v(-26.48, 23) * mm});
            skLineSegment(sketch, "E38.3", {"start": v(-26.48, 23) * mm, "end": v(-16.1, 29) * mm});
            skLineSegment(sketch, "E38.4", {"start": v(-16.1, 29) * mm, "end": v(-5.7, 23) * mm});
            skLineSegment(sketch, "E38.5", {"start": v(-5.7, 23) * mm, "end": v(-5.7, 11) * mm});
            skPoint(sketch, "E38.0.midPoint", {"position": v(-10.9, 8) * mm});
            skCircle(sketch, "E39.cCircle", {"center": v(6.7, 17) * mm, "radius": 10.4 * mm, "construction": true});
            skLineSegment(sketch, "E39.0", {"start": v(17.09, 11) * mm, "end": v(6.7, 5) * mm});
            skLineSegment(sketch, "E39.1", {"start": v(6.7, 5) * mm, "end": v(-3.7, 11) * mm});
            skLineSegment(sketch, "E39.2", {"start": v(-3.7, 11) * mm, "end": v(-3.7, 23) * mm});
            skLineSegment(sketch, "E39.3", {"start": v(-3.7, 23) * mm, "end": v(6.7, 29) * mm});
            skLineSegment(sketch, "E39.4", {"start": v(6.7, 29) * mm, "end": v(17.09, 23) * mm});
            skLineSegment(sketch, "E39.5", {"start": v(17.09, 23) * mm, "end": v(17.09, 11) * mm});
            skPoint(sketch, "E39.0.midPoint", {"position": v(11.9, 8) * mm});
            skCircle(sketch, "E40.cCircle", {"center": v(29.48, 17) * mm, "radius": 10.4 * mm, "construction": true});
            skLineSegment(sketch, "E40.0", {"start": v(39.87, 11) * mm, "end": v(29.48, 5) * mm});
            skLineSegment(sketch, "E40.1", {"start": v(29.48, 5) * mm, "end": v(19.09, 11) * mm});
            skLineSegment(sketch, "E40.2", {"start": v(19.09, 11) * mm, "end": v(19.09, 23) * mm});
            skLineSegment(sketch, "E40.3", {"start": v(19.09, 23) * mm, "end": v(29.48, 29) * mm});
            skLineSegment(sketch, "E40.4", {"start": v(29.48, 29) * mm, "end": v(39.87, 23) * mm});
            skLineSegment(sketch, "E40.5", {"start": v(39.87, 23) * mm, "end": v(39.87, 11) * mm});
            skPoint(sketch, "E40.0.midPoint", {"position": v(34.68, 8) * mm});
            skPoint(sketch, "E41.orphan", {"position": v(-197.37, 30.73) * mm});
            skPoint(sketch, "E42.orphan", {"position": v(-186.97, 24.73) * mm});
            skPoint(sketch, "E43.orphan", {"position": v(51.26, 42.73) * mm});
            skPoint(sketch, "E28.0.start.orphan", {"position": v(51.26, 30.73) * mm});
            skPoint(sketch, "E44.orphan", {"position": v(40.87, 48.73) * mm});
            skPoint(sketch, "E45.orphan", {"position": v(-186.97, 48.73) * mm});
            skLineSegment(sketch, "E46", {"start": v(-185.97, 48.15) * mm, "end": v(-185.97, 25.3) * mm});
            skSolve(sketch);
        }
        {
            var Q0;
            Q0 = qSketchRegion(id + "F7", true);
            extrude(context, id + "F8", {"entities" : qUnion([Q0]), "operationType" : NewBodyOperationType.REMOVE, "oppositeDirection" : true, "depth" : 120 * mm, "offsetDistance" : 25 * mm});
        }
        {
            var Q0;
            Q0=makeQuery(id+"F1.opExtrude","SWEPT_FACE",FACE,{"disambiguationData":[OSD([sQuery(id+"F0.wireOp",EDGE,"E0.bottom")])]});
            var sketch = newSketch(context, id + "F9", { "sketchPlane" : qUnion([Q0])});
            skLineSegment(sketch, "E47", {"start": v(-133.65, 68.46) * mm, "end": v(-133.65, -21.54) * mm, "construction": true});
            skLineSegment(sketch, "E48", {"start": v(-133.65, 68.46) * mm, "end": v(126.35, 68.46) * mm, "construction": true});
            skLineSegment(sketch, "E49", {"start": v(92.35, 68.46) * mm, "end": v(92.35, -21.54) * mm});
            skLineSegment(sketch, "E50.0", {"start": v(-21.73, 50.46) * mm, "end": v(-32.12, 44.46) * mm});
            skLineSegment(sketch, "E50.4", {"start": v(-32.12, 68.46) * mm, "end": v(-21.73, 62.46) * mm});
            skLineSegment(sketch, "E50.5", {"start": v(-21.73, 62.46) * mm, "end": v(-21.73, 50.46) * mm});
            skCircle(sketch, "E51.cCircle", {"center": v(-9.33, 56.46) * mm, "radius": 10.4 * mm, "construction": true});
            skLineSegment(sketch, "E51.0", {"start": v(1.06, 50.46) * mm, "end": v(-9.33, 44.46) * mm});
            skLineSegment(sketch, "E51.1", {"start": v(-9.33, 44.46) * mm, "end": v(-19.73, 50.46) * mm});
            skLineSegment(sketch, "E51.2", {"start": v(-19.73, 50.46) * mm, "end": v(-19.73, 62.46) * mm});
            skLineSegment(sketch, "E51.3", {"start": v(-19.73, 62.46) * mm, "end": v(-9.33, 68.46) * mm});
            skLineSegment(sketch, "E51.4", {"start": v(-9.33, 68.46) * mm, "end": v(1.06, 62.46) * mm});
            skLineSegment(sketch, "E51.5", {"start": v(1.06, 62.46) * mm, "end": v(1.06, 50.46) * mm});
            skPoint(sketch, "E51.0.midPoint", {"position": v(-4.14, 47.46) * mm});
            skCircle(sketch, "E52.cCircle", {"center": v(13.45, 56.46) * mm, "radius": 10.4 * mm, "construction": true});
            skLineSegment(sketch, "E52.0", {"start": v(23.84, 50.46) * mm, "end": v(13.45, 44.46) * mm});
            skLineSegment(sketch, "E52.1", {"start": v(13.45, 44.46) * mm, "end": v(3.06, 50.46) * mm});
            skLineSegment(sketch, "E52.2", {"start": v(3.06, 50.46) * mm, "end": v(3.06, 62.46) * mm});
            skLineSegment(sketch, "E52.3", {"start": v(3.06, 62.46) * mm, "end": v(13.45, 68.46) * mm});
            skLineSegment(sketch, "E52.4", {"start": v(13.45, 68.46) * mm, "end": v(23.84, 62.46) * mm});
            skLineSegment(sketch, "E52.5", {"start": v(23.84, 62.46) * mm, "end": v(23.84, 50.46) * mm});
            skPoint(sketch, "E52.0.midPoint", {"position": v(18.65, 47.46) * mm});
            skLineSegment(sketch, "E53.1", {"start": v(36.23, 44.46) * mm, "end": v(25.84, 50.46) * mm});
            skLineSegment(sketch, "E53.2", {"start": v(25.84, 50.46) * mm, "end": v(25.84, 62.46) * mm});
            skLineSegment(sketch, "E53.3", {"start": v(25.84, 62.46) * mm, "end": v(36.23, 68.46) * mm});
            skCircle(sketch, "E54.cCircle", {"center": v(-20.73, 36.73) * mm, "radius": 10.4 * mm, "construction": true});
            skLineSegment(sketch, "E54.0", {"start": v(-10.33, 30.73) * mm, "end": v(-20.73, 24.73) * mm});
            skLineSegment(sketch, "E54.1", {"start": v(-20.73, 24.73) * mm, "end": v(-31.12, 30.73) * mm});
            skLineSegment(sketch, "E54.3", {"start": v(-31.12, 42.73) * mm, "end": v(-20.73, 48.73) * mm});
            skLineSegment(sketch, "E54.4", {"start": v(-20.73, 48.73) * mm, "end": v(-10.33, 42.73) * mm});
            skLineSegment(sketch, "E54.5", {"start": v(-10.33, 42.73) * mm, "end": v(-10.33, 30.73) * mm});
            skPoint(sketch, "E54.0.midPoint", {"position": v(-15.53, 27.73) * mm});
            skCircle(sketch, "E55.cCircle", {"center": v(2.06, 36.73) * mm, "radius": 10.4 * mm, "construction": true});
            skLineSegment(sketch, "E55.0", {"start": v(12.45, 30.73) * mm, "end": v(2.06, 24.73) * mm});
            skLineSegment(sketch, "E55.1", {"start": v(2.06, 24.73) * mm, "end": v(-8.33, 30.73) * mm});
            skLineSegment(sketch, "E55.2", {"start": v(-8.33, 30.73) * mm, "end": v(-8.33, 42.73) * mm});
            skLineSegment(sketch, "E55.3", {"start": v(-8.33, 42.73) * mm, "end": v(2.06, 48.73) * mm});
            skLineSegment(sketch, "E55.4", {"start": v(2.06, 48.73) * mm, "end": v(12.45, 42.73) * mm});
            skLineSegment(sketch, "E55.5", {"start": v(12.45, 42.73) * mm, "end": v(12.45, 30.73) * mm});
            skPoint(sketch, "E55.0.midPoint", {"position": v(7.25, 27.73) * mm});
            skCircle(sketch, "E56.cCircle", {"center": v(24.84, 36.73) * mm, "radius": 10.4 * mm, "construction": true});
            skLineSegment(sketch, "E56.0", {"start": v(35.23, 30.73) * mm, "end": v(24.84, 24.73) * mm});
            skLineSegment(sketch, "E56.1", {"start": v(24.84, 24.73) * mm, "end": v(14.45, 30.73) * mm});
            skLineSegment(sketch, "E56.2", {"start": v(14.45, 30.73) * mm, "end": v(14.45, 42.73) * mm});
            skLineSegment(sketch, "E56.3", {"start": v(14.45, 42.73) * mm, "end": v(24.84, 48.73) * mm});
            skLineSegment(sketch, "E56.4", {"start": v(24.84, 48.73) * mm, "end": v(35.23, 42.73) * mm});
            skLineSegment(sketch, "E56.5", {"start": v(35.23, 42.73) * mm, "end": v(35.23, 30.73) * mm});
            skPoint(sketch, "E56.0.midPoint", {"position": v(30.04, 27.73) * mm});
            skLineSegment(sketch, "E57", {"start": v(126.35, 48.73) * mm, "end": v(-133.65, 48.73) * mm, "construction": true});
            skLineSegment(sketch, "E58", {"start": v(-137.64, 24.73) * mm, "end": v(127.57, 24.73) * mm, "construction": true});
            skLineSegment(sketch, "E59", {"start": v(-133.65, 29) * mm, "end": v(126.35, 29) * mm, "construction": true});
            skLineSegment(sketch, "E60", {"start": v(-133.65, 5) * mm, "end": v(126.35, 5) * mm, "construction": true});
            skLineSegment(sketch, "E61.0", {"start": v(-21.73, 11) * mm, "end": v(-32.12, 5) * mm});
            skLineSegment(sketch, "E61.4", {"start": v(-32.12, 29) * mm, "end": v(-21.73, 23) * mm});
            skLineSegment(sketch, "E61.5", {"start": v(-21.73, 23) * mm, "end": v(-21.73, 11) * mm});
            skCircle(sketch, "E62.cCircle", {"center": v(-9.33, 17) * mm, "radius": 10.4 * mm, "construction": true});
            skLineSegment(sketch, "E62.0", {"start": v(1.06, 11) * mm, "end": v(-9.33, 5) * mm});
            skLineSegment(sketch, "E62.1", {"start": v(-9.33, 5) * mm, "end": v(-19.73, 11) * mm});
            skLineSegment(sketch, "E62.2", {"start": v(-19.73, 11) * mm, "end": v(-19.73, 23) * mm});
            skLineSegment(sketch, "E62.3", {"start": v(-19.73, 23) * mm, "end": v(-9.33, 29) * mm});
            skLineSegment(sketch, "E62.4", {"start": v(-9.33, 29) * mm, "end": v(1.06, 23) * mm});
            skLineSegment(sketch, "E62.5", {"start": v(1.06, 23) * mm, "end": v(1.06, 11) * mm});
            skPoint(sketch, "E62.0.midPoint", {"position": v(-4.14, 8) * mm});
            skCircle(sketch, "E63.cCircle", {"center": v(13.45, 17) * mm, "radius": 10.4 * mm, "construction": true});
            skLineSegment(sketch, "E63.0", {"start": v(23.84, 11) * mm, "end": v(13.45, 5) * mm});
            skLineSegment(sketch, "E63.1", {"start": v(13.45, 5) * mm, "end": v(3.06, 11) * mm});
            skLineSegment(sketch, "E63.2", {"start": v(3.06, 11) * mm, "end": v(3.06, 23) * mm});
            skLineSegment(sketch, "E63.3", {"start": v(3.06, 23) * mm, "end": v(13.45, 29) * mm});
            skLineSegment(sketch, "E63.4", {"start": v(13.45, 29) * mm, "end": v(23.84, 23) * mm});
            skLineSegment(sketch, "E63.5", {"start": v(23.84, 23) * mm, "end": v(23.84, 11) * mm});
            skPoint(sketch, "E63.0.midPoint", {"position": v(18.65, 8) * mm});
            skLineSegment(sketch, "E64.1", {"start": v(36.23, 5) * mm, "end": v(25.84, 11) * mm});
            skLineSegment(sketch, "E64.2", {"start": v(25.84, 11) * mm, "end": v(25.84, 23) * mm});
            skLineSegment(sketch, "E64.3", {"start": v(25.84, 23) * mm, "end": v(36.23, 29) * mm});
            skLineSegment(sketch, "E65", {"start": v(-32.12, 68.46) * mm, "end": v(-32.12, 5) * mm});
            skLineSegment(sketch, "E66", {"start": v(-31.12, 42.73) * mm, "end": v(-31.12, 30.73) * mm});
            skLineSegment(sketch, "E67", {"start": v(36.23, 68.46) * mm, "end": v(36.23, 5) * mm});
            skSolve(sketch);
        }
        {
            var Q0;
            Q0 = qSketchRegion(id + "F9", true);
            extrude(context, id + "F10", {"entities" : qUnion([Q0]), "operationType" : NewBodyOperationType.REMOVE, "oppositeDirection" : true, "depth" : 260 * mm, "offsetDistance" : 25 * mm});
        }
    });
